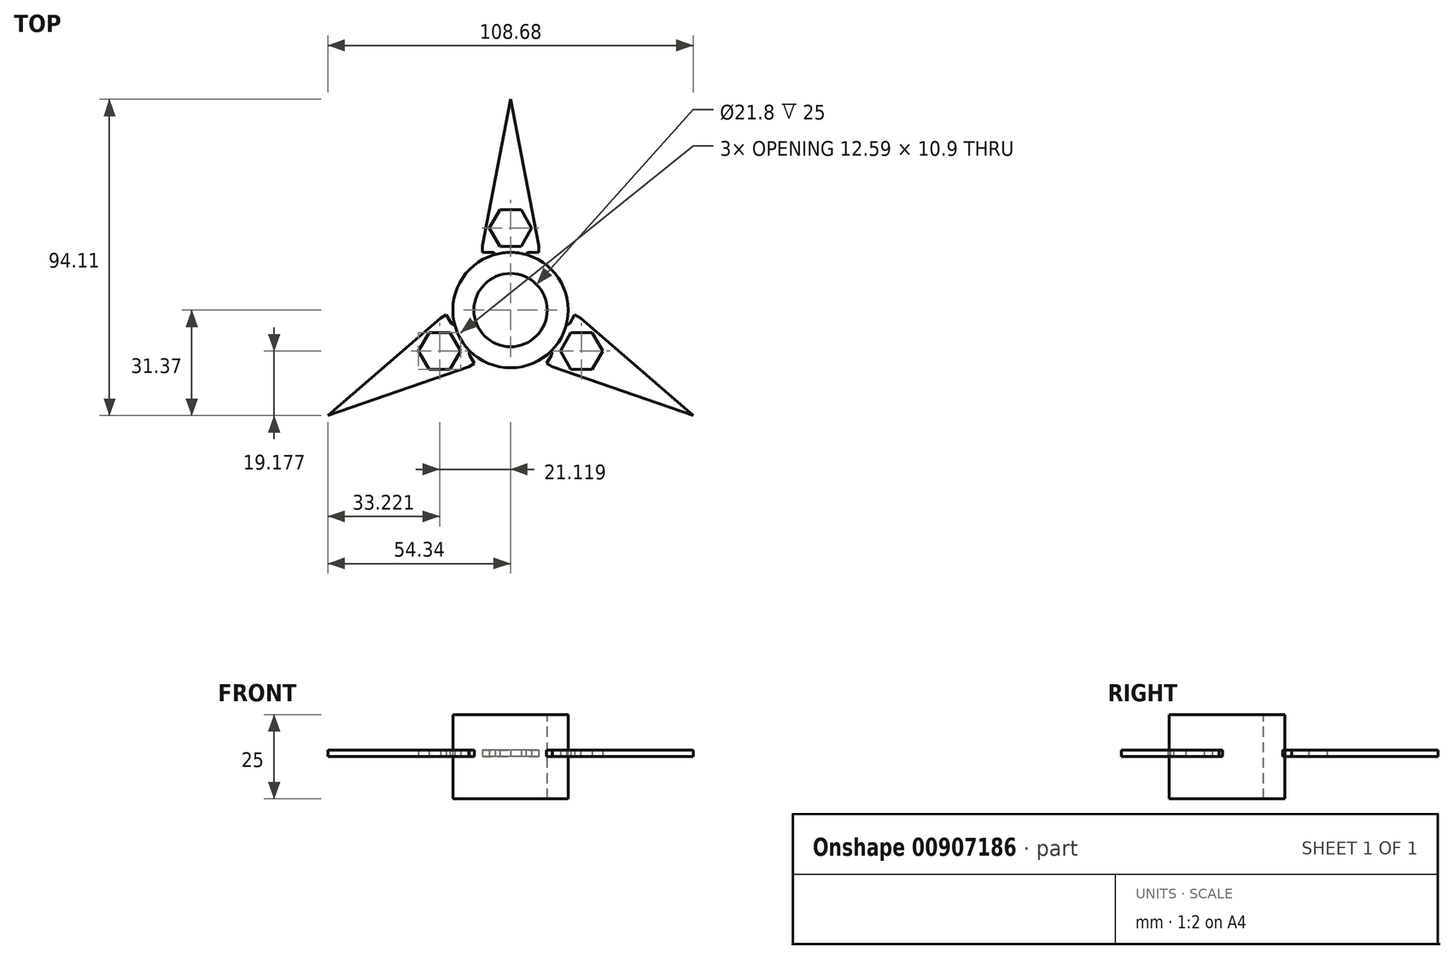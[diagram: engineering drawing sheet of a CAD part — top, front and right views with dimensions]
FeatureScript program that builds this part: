
annotation { "Feature Type Name" : "Feature", "Feature Type Description" : "" }
export const myFeature = defineFeature(function(context is Context, id is Id, definition is map)
    precondition{}
    {
        {
            var Q0;
            Q0=qCreatedBy(makeId("Top.planeOp"),FACE);
            var sketch = newSketch(context, id + "F0", { "sketchPlane" : qUnion([Q0])});
            skCircle(sketch, "E0", {"center": v(0, 0) * mm, "radius": 10.9 * mm});
            skLineSegment(sketch, "E1", {"start": v(-5.5, 17.22) * mm, "end": v(-8.4, 17.22) * mm});
            skLineSegment(sketch, "E2", {"start": v(-8.4, 17.22) * mm, "end": v(-8.4, 19.22) * mm});
            skLineSegment(sketch, "E3", {"start": v(-8.4, 19.22) * mm, "end": v(0, 62.74) * mm});
            skPoint(sketch, "E4.visualSharp", {"position": v(-4.5, 17.22) * mm});
            skArc(sketch, "E4.filletArc", {"start": v(-4.55, 16.55) * mm, "mid": v(-4.92, 17.04) * mm, "end": v(-5.5, 17.22) * mm});
            skLineSegment(sketch, "E5.MirrorCS", {"start": v(8.4, 19.22) * mm, "end": v(0, 62.74) * mm});
            skLineSegment(sketch, "E6.MirrorCS", {"start": v(8.4, 17.22) * mm, "end": v(8.4, 19.22) * mm});
            skLineSegment(sketch, "E7.MirrorCS", {"start": v(5.5, 17.22) * mm, "end": v(8.4, 17.22) * mm});
            skPoint(sketch, "E8.MirrorP", {"position": v(4.5, 17.22) * mm});
            skArc(sketch, "E9.MirrorCS", {"start": v(4.55, 16.55) * mm, "mid": v(4.92, 17.04) * mm, "end": v(5.5, 17.22) * mm});
            skLineSegment(sketch, "E10.1.0", {"start": v(-20.85, -2.33) * mm, "end": v(-54.34, -31.37) * mm});
            skPoint(sketch, "E10.1.1", {"position": v(-17.17, -4.72) * mm});
            skPoint(sketch, "E10.1.4", {"position": v(-12.67, -12.5) * mm});
            skLineSegment(sketch, "E10.1.5", {"start": v(-12.44, -16.89) * mm, "end": v(-54.34, -31.37) * mm});
            skArc(sketch, "E10.1.6", {"start": v(-16.3, -4.22) * mm, "mid": v(-17.06, -4.32) * mm, "end": v(-17.67, -3.85) * mm});
            skLineSegment(sketch, "E10.1.7", {"start": v(-10.71, -15.9) * mm, "end": v(-12.44, -16.89) * mm});
            skLineSegment(sketch, "E10.1.8", {"start": v(-12.17, -13.37) * mm, "end": v(-10.71, -15.9) * mm});
            skLineSegment(sketch, "E10.1.9", {"start": v(-19.12, -1.33) * mm, "end": v(-20.85, -2.33) * mm});
            skLineSegment(sketch, "E10.1.10", {"start": v(-17.67, -3.85) * mm, "end": v(-19.12, -1.33) * mm});
            skArc(sketch, "E10.1.11", {"start": v(-11.8, -12) * mm, "mid": v(-12.27, -12.62) * mm, "end": v(-12.17, -13.37) * mm});
            skLineSegment(sketch, "E10.2.0", {"start": v(12.44, -16.89) * mm, "end": v(54.34, -31.37) * mm});
            skPoint(sketch, "E10.2.1", {"position": v(12.67, -12.5) * mm});
            skPoint(sketch, "E10.2.4", {"position": v(17.17, -4.72) * mm});
            skLineSegment(sketch, "E10.2.5", {"start": v(20.85, -2.33) * mm, "end": v(54.34, -31.37) * mm});
            skArc(sketch, "E10.2.6", {"start": v(11.8, -12) * mm, "mid": v(12.27, -12.62) * mm, "end": v(12.17, -13.37) * mm});
            skLineSegment(sketch, "E10.2.7", {"start": v(19.12, -1.33) * mm, "end": v(20.85, -2.33) * mm});
            skLineSegment(sketch, "E10.2.8", {"start": v(17.67, -3.85) * mm, "end": v(19.12, -1.33) * mm});
            skLineSegment(sketch, "E10.2.9", {"start": v(10.71, -15.9) * mm, "end": v(12.44, -16.89) * mm});
            skLineSegment(sketch, "E10.2.10", {"start": v(12.17, -13.37) * mm, "end": v(10.71, -15.9) * mm});
            skArc(sketch, "E10.2.11", {"start": v(16.3, -4.22) * mm, "mid": v(17.06, -4.32) * mm, "end": v(17.67, -3.85) * mm});
            skCircle(sketch, "E11.cCircle", {"center": v(0, 24.39) * mm, "radius": 5.45 * mm, "construction": true});
            skLineSegment(sketch, "E11.0", {"start": v(3.15, 18.94) * mm, "end": v(-3.15, 18.94) * mm});
            skLineSegment(sketch, "E11.1", {"start": v(-3.15, 18.94) * mm, "end": v(-6.3, 24.39) * mm});
            skLineSegment(sketch, "E11.2", {"start": v(-6.3, 24.39) * mm, "end": v(-3.15, 29.84) * mm});
            skLineSegment(sketch, "E11.3", {"start": v(-3.15, 29.84) * mm, "end": v(3.15, 29.84) * mm});
            skLineSegment(sketch, "E11.4", {"start": v(3.15, 29.84) * mm, "end": v(6.3, 24.39) * mm});
            skLineSegment(sketch, "E11.5", {"start": v(6.3, 24.39) * mm, "end": v(3.15, 18.94) * mm});
            skPoint(sketch, "E11.0.midPoint", {"position": v(0, 18.94) * mm});
            skLineSegment(sketch, "E12.1.0", {"start": v(-27.41, -12.2) * mm, "end": v(-24.27, -6.74) * mm});
            skLineSegment(sketch, "E12.1.1", {"start": v(-24.27, -17.64) * mm, "end": v(-27.41, -12.2) * mm});
            skLineSegment(sketch, "E12.1.2", {"start": v(-17.97, -17.64) * mm, "end": v(-24.27, -17.64) * mm});
            skLineSegment(sketch, "E12.1.3", {"start": v(-14.83, -12.2) * mm, "end": v(-17.97, -17.64) * mm});
            skLineSegment(sketch, "E12.1.4", {"start": v(-17.97, -6.74) * mm, "end": v(-14.83, -12.2) * mm});
            skLineSegment(sketch, "E12.1.5", {"start": v(-24.27, -6.74) * mm, "end": v(-17.97, -6.74) * mm});
            skLineSegment(sketch, "E12.2.0", {"start": v(24.27, -17.64) * mm, "end": v(17.97, -17.64) * mm});
            skLineSegment(sketch, "E12.2.1", {"start": v(27.41, -12.2) * mm, "end": v(24.27, -17.64) * mm});
            skLineSegment(sketch, "E12.2.2", {"start": v(24.27, -6.74) * mm, "end": v(27.41, -12.2) * mm});
            skLineSegment(sketch, "E12.2.3", {"start": v(17.97, -6.74) * mm, "end": v(24.27, -6.74) * mm});
            skLineSegment(sketch, "E12.2.4", {"start": v(14.83, -12.2) * mm, "end": v(17.97, -6.74) * mm});
            skLineSegment(sketch, "E12.2.5", {"start": v(17.97, -17.64) * mm, "end": v(14.83, -12.2) * mm});
            skCircle(sketch, "E13", {"center": v(0, 0) * mm, "radius": 17.17 * mm});
            skPoint(sketch, "E14.orphan", {"position": v(-4.5, 16.22) * mm});
            skPoint(sketch, "E15.orphan", {"position": v(4.5, 16.22) * mm});
            skSolve(sketch);
        }
        {
            var Q0;
            Q0=makeQuery(id+"F0.imprint","IMPRINT",FACE,{"disambiguationData":[TD([[makeQuery(id+"F0.imprint","IMPRINT",EDGE,{"derivedFrom":sQuery(id+"F0.wireOp",EDGE,"E10.1.0")}),1.0]])]});
            var Q1;
            Q1=makeQuery(id+"F0.imprint","IMPRINT",FACE,{"disambiguationData":[TD([[makeQuery(id+"F0.imprint","IMPRINT",EDGE,{"derivedFrom":sQuery(id+"F0.wireOp",EDGE,"E10.2.0")}),1.0]])]});
            var Q2;
            Q2=makeQuery(id+"F0.imprint","IMPRINT",FACE,{"disambiguationData":[TD([[makeQuery(id+"F0.imprint","IMPRINT",EDGE,{"derivedFrom":sQuery(id+"F0.wireOp",EDGE,"E1")}),-1.0]])]});
            extrude(context, id + "F1", {"entities" : qUnion([Q0, Q1, Q2]), "depth" : 2 * mm, "offsetDistance" : 25 * mm});
        }
        {
            var Q0;
            Q0=makeQuery(id+"F0.imprint","IMPRINT",FACE,{"disambiguationData":[TD([[makeQuery(id+"F0.imprint","IMPRINT",EDGE,{"derivedFrom":sQuery(id+"F0.wireOp",EDGE,"E0")}),-1.0]])]});
            extrude(context, id + "F2", {"entities" : qUnion([Q0]), "endBound" : BoundingType.SYMMETRIC, "oppositeDirection" : true, "depth" : 25 * mm, "offsetDistance" : 25 * mm});
        }
    });
